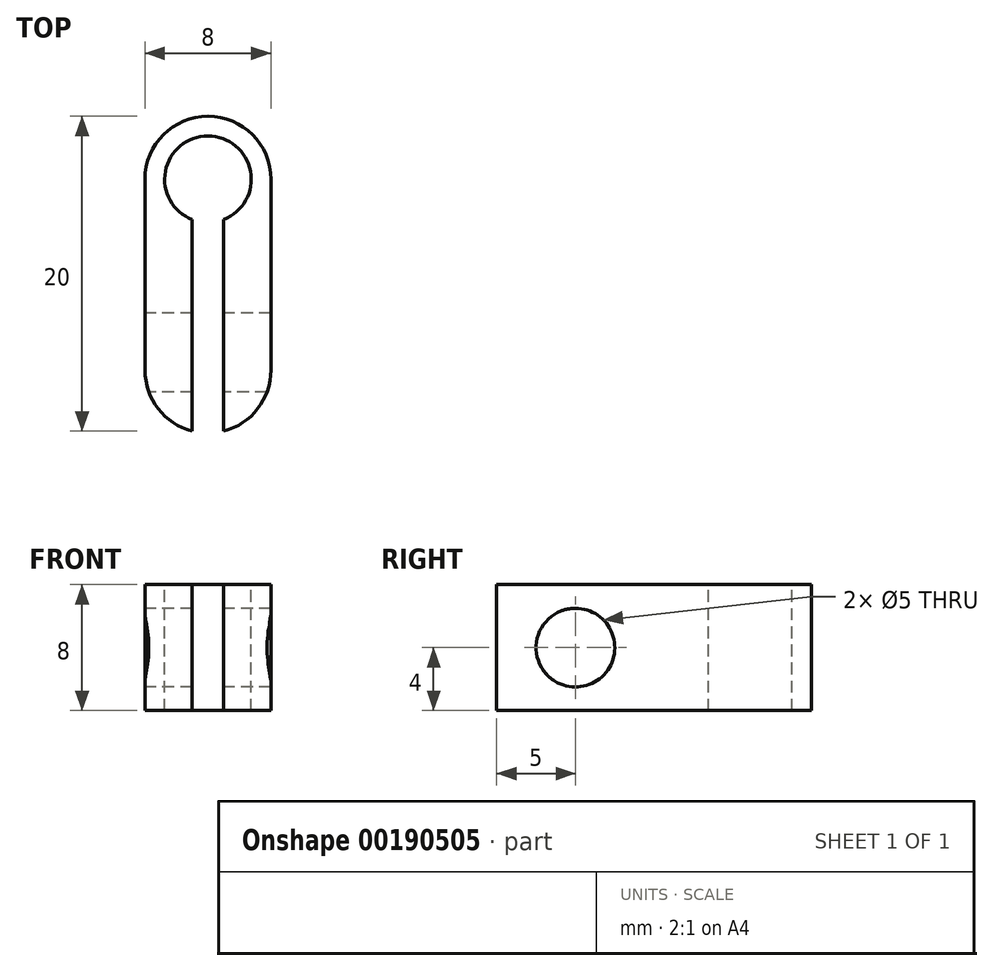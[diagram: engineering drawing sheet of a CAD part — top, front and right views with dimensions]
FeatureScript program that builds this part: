
annotation { "Feature Type Name" : "Feature", "Feature Type Description" : "" }
export const myFeature = defineFeature(function(context is Context, id is Id, definition is map)
    precondition{}
    {
        {
            var Q0;
            Q0=qCreatedBy(makeId("Front.planeOp"),FACE);
            var sketch = newSketch(context, id + "F0", { "sketchPlane" : qUnion([Q0])});
            skLineSegment(sketch, "E0.bottom", {"start": v(0, 0) * mm, "end": v(8, 0) * mm});
            skLineSegment(sketch, "E0.top", {"start": v(0, 8) * mm, "end": v(8, 8) * mm});
            skLineSegment(sketch, "E0.left", {"start": v(0, 0) * mm, "end": v(0, 8) * mm});
            skLineSegment(sketch, "E0.right", {"start": v(8, 0) * mm, "end": v(8, 8) * mm});
            skSolve(sketch);
        }
        {
            var Q0;
            Q0=makeQuery(id+"F0.imprint","IMPRINT",FACE,{"disambiguationData":[TD([[makeQuery(id+"F0.imprint","IMPRINT",EDGE,{"derivedFrom":sQuery(id+"F0.wireOp",EDGE,"E0.bottom")}),1.0]])]});
            extrude(context, id + "F1", {"entities" : qUnion([Q0]), "depth" : 20 * mm});
        }
        {
            var Q0;
            Q0=makeQuery(id+"F1.opExtrude","CAP_EDGE",EDGE,{"disambiguationData":[OSD([sQuery(id+"F0.wireOp",EDGE,"E0.right")])],"isStart":true});
            var Q1;
            Q1=makeQuery(id+"F1.opExtrude","CAP_EDGE",EDGE,{"disambiguationData":[OSD([sQuery(id+"F0.wireOp",EDGE,"E0.left")])],"isStart":true});
            fillet(context, id + "F2", {"entities" : qUnion([Q0, Q1]), "radius" : 4 * mm, "tangentPropagation" : true, "allowEdgeOverflow" : false});
        }
        {
            var Q0;
            Q0=makeQuery(id+"F1.opExtrude","SWEPT_FACE",FACE,{"disambiguationData":[OSD([sQuery(id+"F0.wireOp",EDGE,"E0.top")])]});
            var sketch = newSketch(context, id + "F3", { "sketchPlane" : qUnion([Q0])});
            skArc(sketch, "E1", {"start": v(5, -6.56) * mm, "mid": v(4, -1.25) * mm, "end": v(3, -6.56) * mm});
            skLineSegment(sketch, "E2.top", {"start": v(4, -20) * mm, "end": v(5, -20) * mm});
            skLineSegment(sketch, "E2.right", {"start": v(5, -6.56) * mm, "end": v(5, -20) * mm});
            skLineSegment(sketch, "E3.top", {"start": v(4, -20) * mm, "end": v(3, -20) * mm});
            skLineSegment(sketch, "E3.right", {"start": v(3, -6.56) * mm, "end": v(3, -20) * mm});
            skPoint(sketch, "E4.orphan", {"position": v(4, -20) * mm});
            skSolve(sketch);
        }
        {
            var Q0;
            Q0=makeQuery(id+"F3.imprint","IMPRINT",FACE,{"disambiguationData":[TD([[makeQuery(id+"F3.imprint","IMPRINT",EDGE,{"derivedFrom":sQuery(id+"F3.wireOp",EDGE,"E1")}),1.0]])]});
            extrude(context, id + "F4", {"entities" : qUnion([Q0]), "operationType" : NewBodyOperationType.REMOVE, "oppositeDirection" : true, "depth" : 25 * mm});
        }
        {
            var Q0;
            Q0=makeQuery(id+"F1.opExtrude","SWEPT_FACE",FACE,{"disambiguationData":[OSD([sQuery(id+"F0.wireOp",EDGE,"E0.left")])]});
            var sketch = newSketch(context, id + "F5", { "sketchPlane" : qUnion([Q0])});
            skCircle(sketch, "E5", {"center": v(15, 4) * mm, "radius": 2.5 * mm});
            skPoint(sketch, "E5.centerSnap0", {"position": v(4, 4) * mm});
            skSolve(sketch);
        }
        {
            var Q0;
            Q0=makeQuery(id+"F1.opExtrude","CAP_EDGE",EDGE,{"disambiguationData":[OSD([sQuery(id+"F0.wireOp",EDGE,"E0.left")])],"isStart":false});
            var Q1;
            Q1=makeQuery(id+"F1.opExtrude","CAP_EDGE",EDGE,{"disambiguationData":[OSD([sQuery(id+"F0.wireOp",EDGE,"E0.right")])],"isStart":false});
            fillet(context, id + "F6", {"entities" : qUnion([Q0, Q1]), "radius" : 4 * mm, "tangentPropagation" : true, "allowEdgeOverflow" : false});
        }
        {
            var Q0;
            Q0=makeQuery(id+"F5.imprint","IMPRINT",FACE,{"disambiguationData":[TD([[makeQuery(id+"F5.imprint","IMPRINT",EDGE,{"derivedFrom":sQuery(id+"F5.wireOp",EDGE,"E5")}),1.0]])]});
            extrude(context, id + "F7", {"entities" : qUnion([Q0]), "operationType" : NewBodyOperationType.REMOVE, "oppositeDirection" : true, "depth" : 25 * mm});
        }
    });
